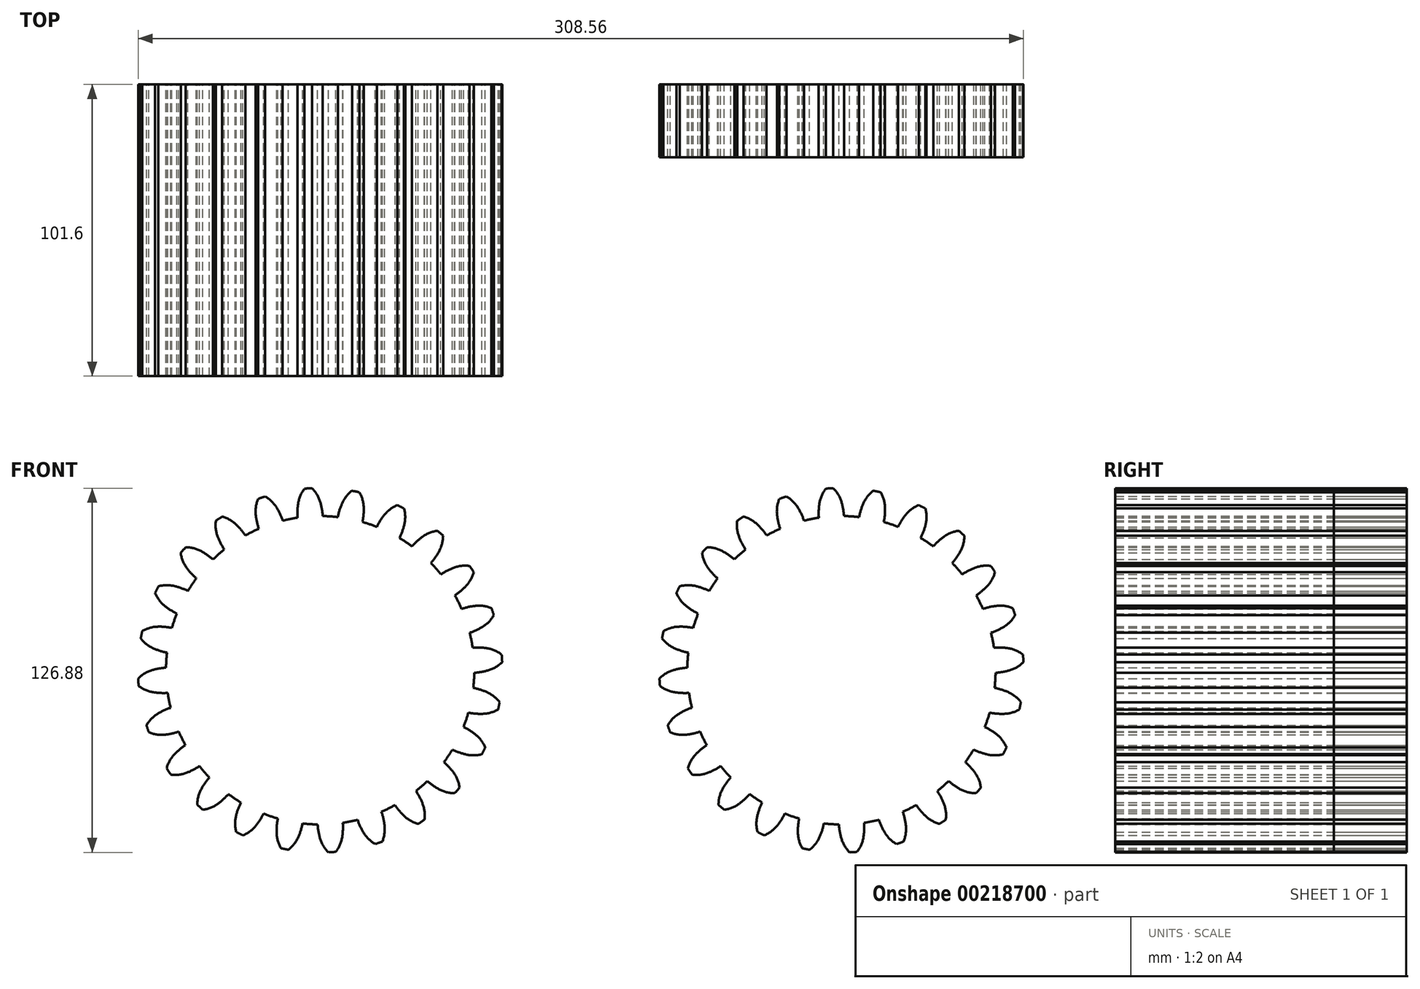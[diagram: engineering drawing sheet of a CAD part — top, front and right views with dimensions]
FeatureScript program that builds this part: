
annotation { "Feature Type Name" : "Feature", "Feature Type Description" : "" }
export const myFeature = defineFeature(function(context is Context, id is Id, definition is map)
    precondition{}
    {
        {
            var Q0;
            Q0=qCreatedBy(makeId("Front.planeOp"),FACE);
            var sketch = newSketch(context, id + "F0", { "sketchPlane" : qUnion([Q0])});
            skCircle(sketch, "E0", {"center": v(0, 0) * mm, "radius": 53.72 * mm});
            skCircle(sketch, "E1", {"center": v(0, 0) * mm, "radius": 58.67 * mm, "construction": true});
            skCircle(sketch, "E2", {"center": v(0, 0) * mm, "radius": 63.5 * mm, "construction": true});
            skLineSegment(sketch, "E3", {"start": v(0, 0) * mm, "end": v(0, 74.22) * mm, "construction": true});
            skLineSegment(sketch, "E4", {"start": v(0, 0) * mm, "end": v(-5.38, 82.08) * mm, "construction": true});
            skLineSegment(sketch, "E5", {"start": v(0, 58.67) * mm, "end": v(-59.73, 58.67) * mm, "construction": true});
            skLineSegment(sketch, "E6", {"start": v(0, 58.67) * mm, "end": v(-65.68, 34.77) * mm, "construction": true});
            skCircle(sketch, "E7", {"center": v(0, 58.67) * mm, "radius": 14.6 * mm, "construction": true});
            skCircle(sketch, "E8", {"center": v(-13.72, 53.68) * mm, "radius": 14.6 * mm, "construction": true});
            skCircle(sketch, "E9", {"center": v(0, 0) * mm, "radius": 55.4 * mm, "construction": true});
            skArc(sketch, "E10", {"start": v(0, 58.67) * mm, "mid": v(-1.13, 61.23) * mm, "end": v(-2.86, 63.44) * mm});
            skArc(sketch, "E11", {"start": v(0.88, 53.71) * mm, "mid": v(0.58, 56.22) * mm, "end": v(0, 58.67) * mm});
            skArc(sketch, "E12.MirrorCS", {"start": v(-7.66, 58.17) * mm, "mid": v(-6.87, 60.86) * mm, "end": v(-5.45, 63.27) * mm});
            skArc(sketch, "E13.MirrorCS", {"start": v(-7.88, 53.14) * mm, "mid": v(-7.92, 55.66) * mm, "end": v(-7.66, 58.17) * mm});
            skArc(sketch, "E14", {"start": v(-2.86, 63.44) * mm, "mid": v(-4.15, 63.36) * mm, "end": v(-5.45, 63.27) * mm});
            skSolve(sketch);
        }
        {
            var Q0;
            Q0 = qSketchRegion(id + "F0", true);
            extrude(context, id + "F1", {"entities" : qUnion([Q0]), "depth" : 25.4 * mm});
        }
        {
            var Q0;
            Q0=makeQuery(id+"F1.opExtrude","SWEPT_BODY",BODY,{"disambiguationData":[OSD([sQuery(id+"F0.wireOp",EDGE,"E0"),sQuery(id+"F0.wireOp",EDGE,"E10"),sQuery(id+"F0.wireOp",EDGE,"E11"),sQuery(id+"F0.wireOp",EDGE,"E12.MirrorCS"),sQuery(id+"F0.wireOp",EDGE,"E13.MirrorCS"),sQuery(id+"F0.wireOp",EDGE,"E14")])]});
            var Q1;
            Q1=makeQuery(id+"F1.opExtrude","SWEPT_FACE",FACE,{"disambiguationData":[OSD([sQuery(id+"F0.wireOp",EDGE,"E10")])]});
            var Q2;
            Q2=makeQuery(id+"F1.opExtrude","SWEPT_FACE",FACE,{"disambiguationData":[OSD([sQuery(id+"F0.wireOp",EDGE,"E14")])]});
            var Q3;
            Q3=makeQuery(id+"F1.opExtrude","SWEPT_FACE",FACE,{"disambiguationData":[OSD([sQuery(id+"F0.wireOp",EDGE,"E11")])]});
            var Q4;
            Q4=makeQuery(id+"F1.opExtrude","SWEPT_FACE",FACE,{"disambiguationData":[OSD([sQuery(id+"F0.wireOp",EDGE,"E13.MirrorCS")])]});
            var Q5;
            Q5=makeQuery(id+"F1.opExtrude","SWEPT_FACE",FACE,{"disambiguationData":[OSD([sQuery(id+"F0.wireOp",EDGE,"E12.MirrorCS")])]});
            var Q6;
            Q6=makeQuery(id+"F1.opExtrude","SWEPT_FACE",FACE,{"disambiguationData":[OSD([sQuery(id+"F0.wireOp",EDGE,"E0")])]});
            circularPattern(context, id + "F2", {"patternType" : PatternType.FACE, "faces" : qUnion([Q1, Q2, Q3, Q4, Q5]), "axis" : qUnion([Q6]), "angle" : 360 * degree, "instanceCount" : 24, "equalSpace" : true});
        }
        {
            var Q0;
            Q0=qCreatedBy(makeId("Front.planeOp"),FACE);
            var sketch = newSketch(context, id + "F3", { "sketchPlane" : qUnion([Q0])});
            skCircle(sketch, "E15", {"center": v(-181.68, 0) * mm, "radius": 53.72 * mm});
            skCircle(sketch, "E16", {"center": v(-181.68, 0) * mm, "radius": 58.67 * mm, "construction": true});
            skCircle(sketch, "E17", {"center": v(-181.68, 0) * mm, "radius": 63.5 * mm, "construction": true});
            skLineSegment(sketch, "E18", {"start": v(-181.68, 0) * mm, "end": v(-181.68, 34.68) * mm, "construction": true});
            skLineSegment(sketch, "E19", {"start": v(-181.68, 0) * mm, "end": v(-183.67, 30.42) * mm, "construction": true});
            skLineSegment(sketch, "E20", {"start": v(-53.16, 58.67) * mm, "end": v(-181.68, 58.67) * mm, "construction": true});
            skLineSegment(sketch, "E21", {"start": v(-93.84, 90.65) * mm, "end": v(-181.68, 58.67) * mm, "construction": true});
            skCircle(sketch, "E22", {"center": v(-181.68, 58.67) * mm, "radius": 14.6 * mm, "construction": true});
            skCircle(sketch, "E23", {"center": v(-195.4, 53.68) * mm, "radius": 14.6 * mm, "construction": true});
            skCircle(sketch, "E24", {"center": v(-181.68, 0) * mm, "radius": 55.4 * mm, "construction": true});
            skArc(sketch, "E25", {"start": v(-181.68, 58.67) * mm, "mid": v(-182.8, 61.23) * mm, "end": v(-184.54, 63.44) * mm});
            skArc(sketch, "E26", {"start": v(-180.8, 53.71) * mm, "mid": v(-181.1, 56.22) * mm, "end": v(-181.68, 58.67) * mm});
            skArc(sketch, "E27.MirrorCS", {"start": v(-189.34, 58.17) * mm, "mid": v(-188.55, 60.86) * mm, "end": v(-187.13, 63.27) * mm});
            skArc(sketch, "E28.MirrorCS", {"start": v(-189.56, 53.14) * mm, "mid": v(-189.6, 55.66) * mm, "end": v(-189.34, 58.17) * mm});
            skArc(sketch, "E29", {"start": v(-184.54, 63.44) * mm, "mid": v(-185.83, 63.36) * mm, "end": v(-187.13, 63.27) * mm});
            skSolve(sketch);
        }
        {
            var Q0;
            Q0 = qSketchRegion(id + "F3", true);
            extrude(context, id + "F4", {"entities" : qUnion([Q0]), "depth" : 101.6 * mm});
        }
        {
            var Q0;
            Q0=makeQuery(id+"F4.opExtrude","SWEPT_FACE",FACE,{"disambiguationData":[OSD([sQuery(id+"F3.wireOp",EDGE,"E28.MirrorCS")])]});
            var Q1;
            Q1=makeQuery(id+"F4.opExtrude","SWEPT_FACE",FACE,{"disambiguationData":[OSD([sQuery(id+"F3.wireOp",EDGE,"E27.MirrorCS")])]});
            var Q2;
            Q2=makeQuery(id+"F4.opExtrude","SWEPT_FACE",FACE,{"disambiguationData":[OSD([sQuery(id+"F3.wireOp",EDGE,"E29")])]});
            var Q3;
            Q3=makeQuery(id+"F4.opExtrude","SWEPT_FACE",FACE,{"disambiguationData":[OSD([sQuery(id+"F3.wireOp",EDGE,"E25")])]});
            var Q4;
            Q4=makeQuery(id+"F4.opExtrude","SWEPT_FACE",FACE,{"disambiguationData":[OSD([sQuery(id+"F3.wireOp",EDGE,"E26")])]});
            var Q5;
            Q5=makeQuery(id+"F4.opExtrude","SWEPT_FACE",FACE,{"disambiguationData":[OSD([sQuery(id+"F3.wireOp",EDGE,"E15")])]});
            circularPattern(context, id + "F5", {"patternType" : PatternType.FACE, "faces" : qUnion([Q0, Q1, Q2, Q3, Q4]), "axis" : qUnion([Q5]), "angle" : 360 * degree, "instanceCount" : 24, "equalSpace" : true});
        }
    });
